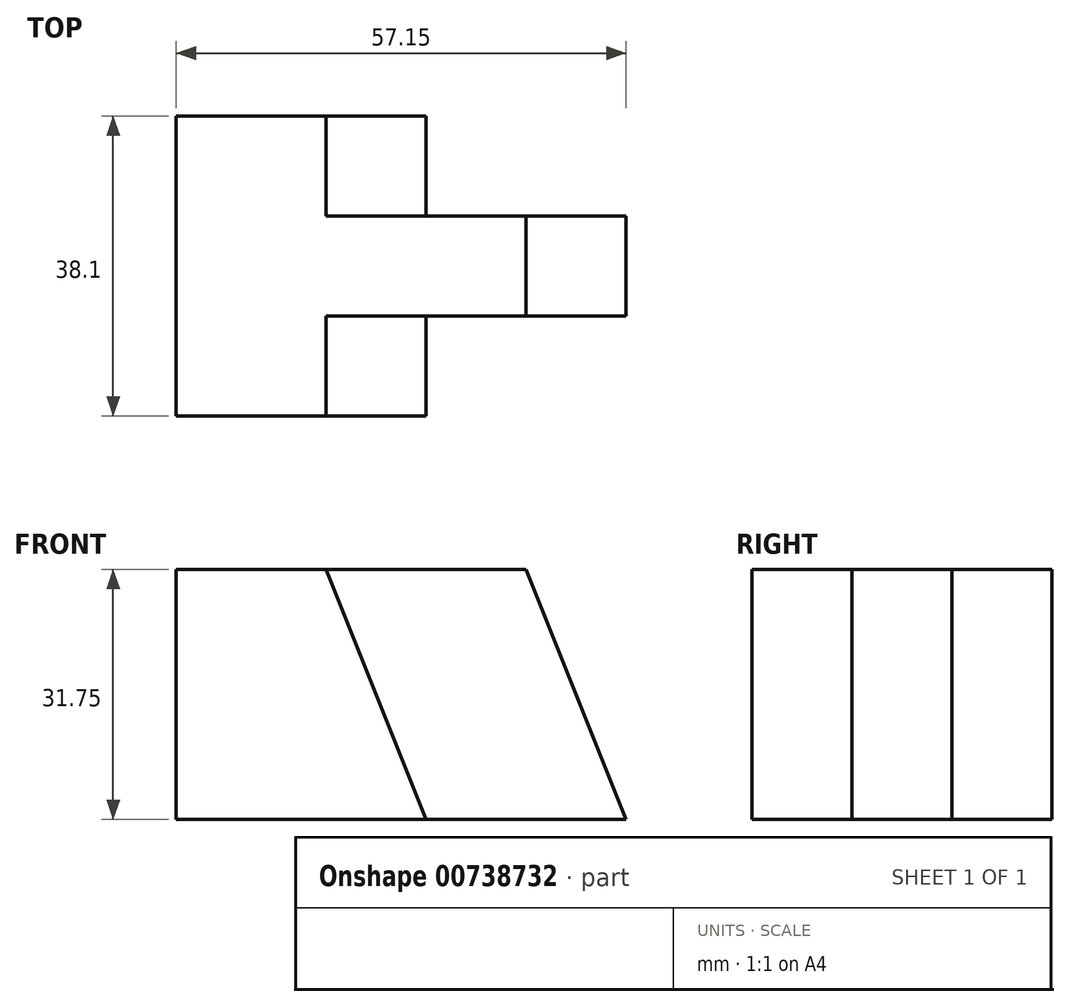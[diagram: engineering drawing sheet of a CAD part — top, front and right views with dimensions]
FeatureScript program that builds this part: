
annotation { "Feature Type Name" : "Feature", "Feature Type Description" : "" }
export const myFeature = defineFeature(function(context is Context, id is Id, definition is map)
    precondition{}
    {
        {
            var Q0;
            Q0=qCreatedBy(makeId("Top.planeOp"),FACE);
            var sketch = newSketch(context, id + "F0", { "sketchPlane" : qUnion([Q0])});
            skLineSegment(sketch, "E0", {"start": v(0, 0) * mm, "end": v(0, 38.1) * mm});
            skLineSegment(sketch, "E1", {"start": v(0, 38.1) * mm, "end": v(57.15, 38.1) * mm});
            skLineSegment(sketch, "E2", {"start": v(57.15, 38.1) * mm, "end": v(57.15, 0) * mm});
            skLineSegment(sketch, "E3", {"start": v(57.15, 0) * mm, "end": v(0, 0) * mm});
            skSolve(sketch);
        }
        {
            var Q0;
            Q0 = qSketchRegion(id + "F0", true);
            extrude(context, id + "F1", {"entities" : qUnion([Q0]), "depth" : 31.75 * mm, "offsetDistance" : 25.4 * mm});
        }
        {
            var Q0;
            Q0=makeQuery(id+"F1.opExtrude","SWEPT_FACE",FACE,{"disambiguationData":[OSD([sQuery(id+"F0.wireOp",EDGE,"E3")])]});
            var sketch = newSketch(context, id + "F2", { "sketchPlane" : qUnion([Q0])});
            skLineSegment(sketch, "E4", {"start": v(19.05, 31.75) * mm, "end": v(31.75, 0) * mm});
            skSolve(sketch);
        }
        {
            var Q0;
            {var subQ0=sQuery(id+"F2.wireOp",EDGE,"E4");Q0=makeQuery(id+"F2.imprint","IMPRINT",FACE,{"disambiguationData":[TD([[makeQuery(id+"F2.imprint","IMPRINT",EDGE,{"derivedFrom":subQ0}),1.0]])]});}
            extrude(context, id + "F3", {"entities" : qUnion([Q0]), "operationType" : NewBodyOperationType.REMOVE, "oppositeDirection" : true, "depth" : 12.7 * mm, "offsetDistance" : 25.4 * mm});
        }
        {
            var Q0;
            Q0=makeQuery(id+"F1.opExtrude","SWEPT_FACE",FACE,{"disambiguationData":[OSD([sQuery(id+"F0.wireOp",EDGE,"E1")])]});
            var sketch = newSketch(context, id + "F4", { "sketchPlane" : qUnion([Q0])});
            skLineSegment(sketch, "E5", {"start": v(-31.75, 0) * mm, "end": v(-19.05, 31.75) * mm});
            skSolve(sketch);
        }
        {
            var Q0;
            {var subQ0=sQuery(id+"F4.wireOp",EDGE,"E5");Q0=makeQuery(id+"F4.imprint","IMPRINT",FACE,{"disambiguationData":[TD([[makeQuery(id+"F4.imprint","IMPRINT",EDGE,{"derivedFrom":subQ0}),1.0]])]});}
            extrude(context, id + "F5", {"entities" : qUnion([Q0]), "operationType" : NewBodyOperationType.REMOVE, "oppositeDirection" : true, "depth" : 12.7 * mm, "offsetDistance" : 25.4 * mm});
        }
        {
            var Q0;
            Q0=makeQuery(id+"F3.boolean.opBoolean","COPY",FACE,{"derivedFrom":makeQuery(id+"F3.opExtrude","CAP_FACE",FACE,{"disambiguationData":[OSD([sQuery(id+"F0.wireOp",EDGE,"E2"),sQuery(id+"F0.wireOp",EDGE,"E3"),sQuery(id+"F2.wireOp",EDGE,"E4")])],"isStart":false})});
            var sketch = newSketch(context, id + "F6", { "sketchPlane" : qUnion([Q0])});
            skLineSegment(sketch, "E6", {"start": v(57.15, 0) * mm, "end": v(44.45, 31.75) * mm});
            skSolve(sketch);
        }
        {
            var Q0;
            {var subQ0=sQuery(id+"F6.wireOp",EDGE,"E6");Q0=makeQuery(id+"F6.imprint","IMPRINT",FACE,{"disambiguationData":[TD([[makeQuery(id+"F6.imprint","IMPRINT",EDGE,{"derivedFrom":subQ0}),-1.0]])]});}
            extrude(context, id + "F7", {"entities" : qUnion([Q0]), "operationType" : NewBodyOperationType.REMOVE, "oppositeDirection" : true, "depth" : 25.4 * mm, "offsetDistance" : 25.4 * mm});
        }
    });
